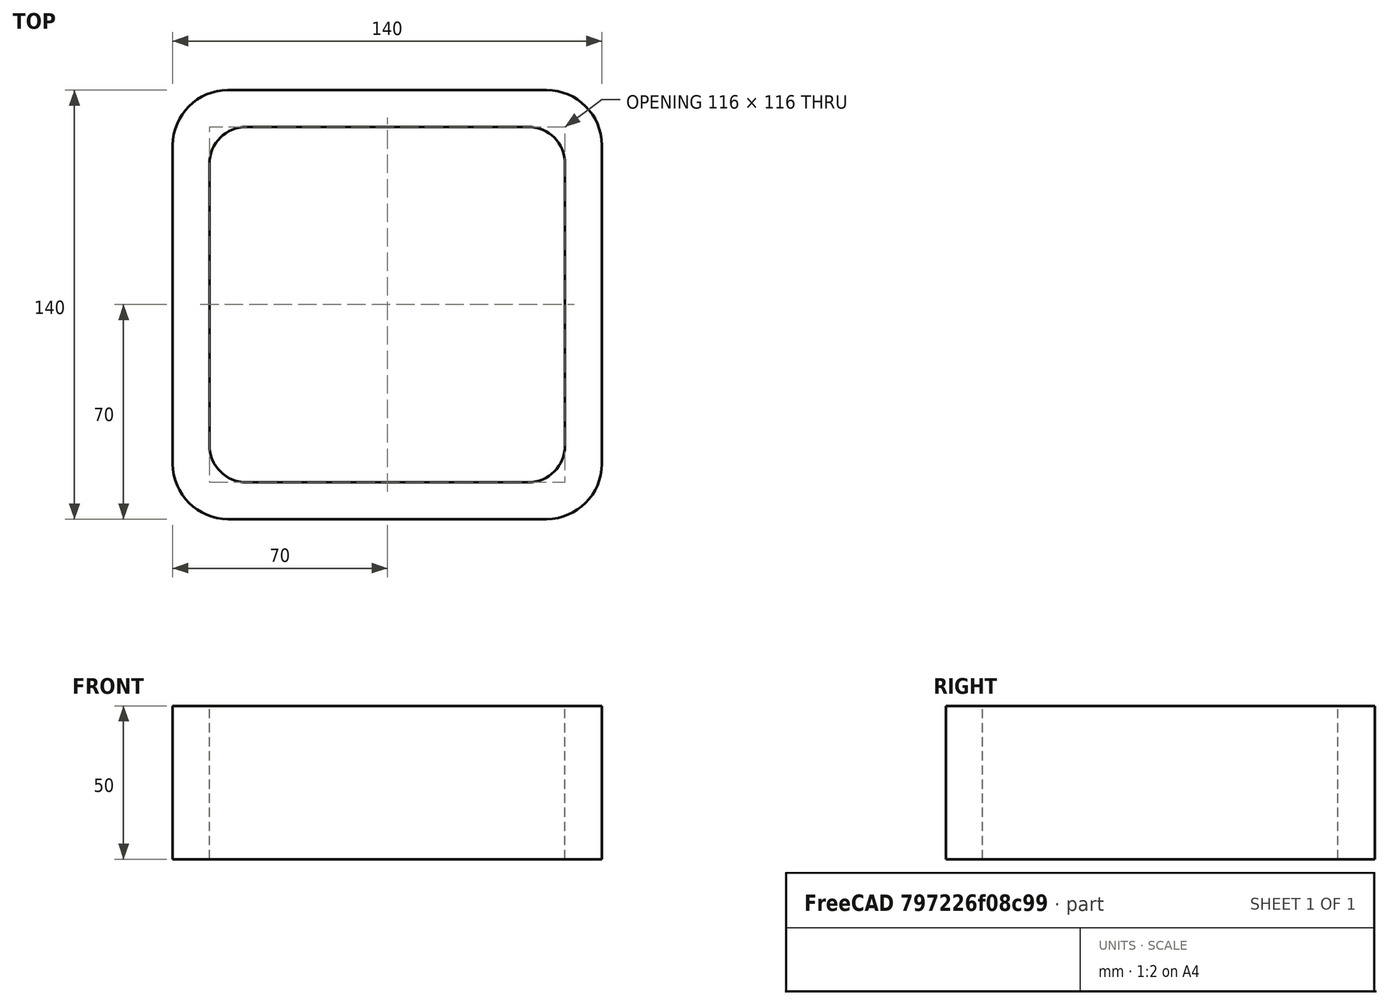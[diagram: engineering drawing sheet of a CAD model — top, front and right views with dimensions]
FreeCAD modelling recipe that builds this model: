
FCSTD DOCUMENT  (FreeCAD 0.15R4671 (Git))
Label: Square hollow section 140x140x12 EN10219 S235JRH
License: All rights reserved
LicenseURL: http://en.wikipedia.org/wiki/All_rights_reserved
objects: Sketcher::SketchObject×1, Part::Extrusion×1
note: 2 computed .brp shape members not serialized (recipe doc carries the construction recipe); baked Part::Feature solids carry a one-line shape summary decoded from their .brp

FEATURE [Sketcher::SketchObject] Sketch
  sketch-geometry (16):
    g0: LineSegment StartX=-46 StartY=58 StartZ=0 EndX=46 EndY=58 EndZ=0
    g1: LineSegment StartX=58 StartY=46 StartZ=0 EndX=58 EndY=-46 EndZ=0
    g2: LineSegment StartX=46 StartY=-58 StartZ=0 EndX=-46 EndY=-58 EndZ=0
    g3: LineSegment StartX=-58 StartY=-46 StartZ=0 EndX=-58 EndY=46 EndZ=0
    g4: LineSegment StartX=-52 StartY=70 StartZ=0 EndX=52 EndY=70 EndZ=0
    g5: LineSegment StartX=70 StartY=52 StartZ=0 EndX=70 EndY=-52 EndZ=0
    g6: LineSegment StartX=52 StartY=-70 StartZ=0 EndX=-52 EndY=-70 EndZ=0
    g7: LineSegment StartX=-70 StartY=-52 StartZ=0 EndX=-70 EndY=52 EndZ=0
    g8: ArcOfCircle CenterX=-46 CenterY=46 CenterZ=0 NormalX=0 NormalY=0 NormalZ=1 Radius=12 StartAngle=1.5708 EndAngle=3.14159
    g9: ArcOfCircle CenterX=46 CenterY=46 CenterZ=0 NormalX=0 NormalY=0 NormalZ=1 Radius=12 StartAngle=0 EndAngle=1.5708
    g10: ArcOfCircle CenterX=46 CenterY=-46 CenterZ=0 NormalX=0 NormalY=0 NormalZ=1 Radius=12 StartAngle=4.71239 EndAngle=6.28319
    g11: ArcOfCircle CenterX=-46 CenterY=-46 CenterZ=0 NormalX=0 NormalY=0 NormalZ=1 Radius=12 StartAngle=3.14159 EndAngle=4.71239
    g12: ArcOfCircle CenterX=52 CenterY=52 CenterZ=0 NormalX=0 NormalY=0 NormalZ=1 Radius=18 StartAngle=0 EndAngle=1.5708
    g13: ArcOfCircle CenterX=52 CenterY=-52 CenterZ=0 NormalX=0 NormalY=0 NormalZ=1 Radius=18 StartAngle=4.71239 EndAngle=6.28319
    g14: ArcOfCircle CenterX=-52 CenterY=-52 CenterZ=0 NormalX=0 NormalY=0 NormalZ=1 Radius=18 StartAngle=3.14159 EndAngle=4.71239
    g15: ArcOfCircle CenterX=-52 CenterY=52 CenterZ=0 NormalX=0 NormalY=0 NormalZ=1 Radius=18 StartAngle=1.5708 EndAngle=3.14159
  constraints (36):
    c: Horizontal(g2)
    c: Vertical(g3)
    c: Horizontal(g6)
    c: Vertical(g7)
    c: Tangent(g3,g8) = 1.5708
    c: Tangent(g0,g8) = 1.5708
    c: Tangent(g0,g9) = 1.5708
    c: Tangent(g1,g9) = 1.5708
    c: Tangent(g1,g10) = 1.5708
    c: Tangent(g2,g10) = 1.5708
    c: Tangent(g2,g11) = 1.5708
    c: Tangent(g3,g11) = 1.5708
    c: Tangent(g4,g12) = 1.5708
    c: Tangent(g5,g12) = 1.5708
    c: Tangent(g5,g13) = 1.5708
    c: Tangent(g6,g13) = 1.5708
    c: Tangent(g6,g14) = 1.5708
    c: Tangent(g7,g14) = 1.5708
    c: Tangent(g7,g15) = 1.5708
    c: Tangent(g4,g15) = 1.5708
    c: Equal(g9,g8)
    c: Equal(g9,g11)
    c: Equal(g9,g10)
    c: Equal(g12,g15)
    c: Equal(g12,g14)
    c: Equal(g12,g13)
    c: Symmetric(g4,g6,g-1)
    c: Symmetric(g7,g5,g-2)
    c: DistanceY(g4,g6) = -140
    c: DistanceX(g7,g5) = 140
    c: Symmetric(g3,g1,g-2)
    c: Symmetric(g0,g2,g-1)
    c: DistanceY(g0,g4) = 12
    c: DistanceX(g5,g1) = -12
    c: Radius(g9) = 12
    c: Radius(g12) = 18
FEATURE [Part::Extrusion] Extrude  label="Square hollow section 140x140x12 EN10219 S235JRH"
  Base = -> Sketch
  Dir = (0,0,50)
  Solid = true
